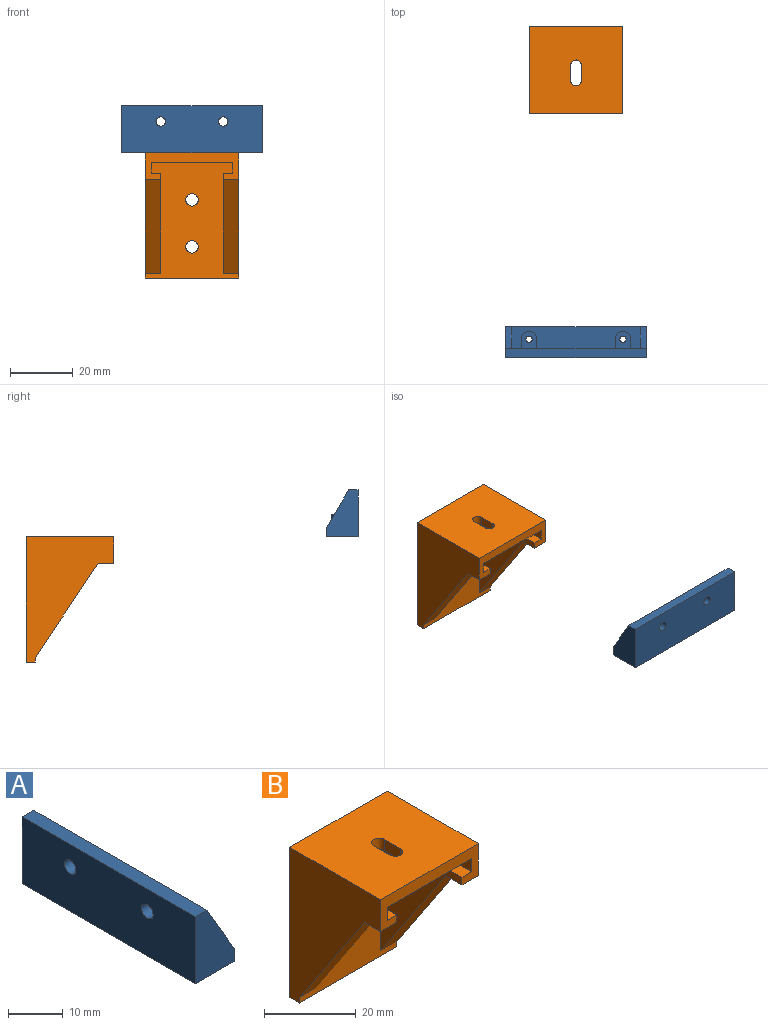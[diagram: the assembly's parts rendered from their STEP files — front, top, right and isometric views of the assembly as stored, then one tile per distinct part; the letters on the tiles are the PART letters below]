
ASSEMBLY  parts=2 mates=1
PART A: 24 faces, bbox 10x45x15 mm
  f0: plane 41x7mm, normal (0,0,1), area 237.4mm2, adj f1,f5,f12,f13,f14,f16,f17,f18
  f1: plane 41x12mm, normal (1,0,0), area 437.9mm2, adj f0,f2,f8,f9,f13,f14,f15,f16
  f2: plane 45x3mm, normal (0,0,1), area 135mm2, adj f1,f3,f6,f7,f20,f22
  f3: plane 45x15mm, normal (-1,0,0), area 660.9mm2, adj f2,f4,f6,f7,f8,f9
  f4: plane 45x10mm, normal (0,0,-1), area 443.7mm2, adj f3,f5,f6,f7,f10,f11
  f5: plane 45x3mm, normal (1,0,0), area 135mm2, adj f0,f4,f6,f7,f20,f22
  f6: plane 15x10mm, normal (0,-1,0), area 108mm2, adj f2,f3,f4,f5,f20
  f7: plane 15x10mm, normal (0,1,0), area 108mm2, adj f2,f3,f4,f5,f22
  f8: cylinder r=1.5mm len=3mm, axis (1,0,0), area 28.3mm2, adj f1,f3
  f9: cylinder r=1.5mm len=3mm, axis (1,0,0), area 28.3mm2, adj f1,f3
  f10: cylinder r=1mm len=7mm, axis (0,0,1), area 44mm2, adj f4,f19
  f11: cylinder r=1mm len=7mm, axis (0,0,1), area 44mm2, adj f4,f15
  f12: cylinder r=2.5mm len=5mm, axis (0,0,-1), area 31.4mm2, adj f0,f13,f14,f15
  f13: plane 4x3mm, normal (0,1,0), area 12mm2, adj f0,f1,f12,f15
  f14: plane 4x3mm, normal (0,-1,0), area 12mm2, adj f0,f1,f12,f15
  f15: plane 5.5x5mm, normal (0,0,1), area 21.7mm2, adj f1,f11,f12,f13,f14
  f16: plane 4x3mm, normal (0,-1,0), area 12mm2, adj f0,f1,f17,f19
  f17: cylinder r=2.5mm len=5mm, axis (0,0,-1), area 31.4mm2, adj f0,f16,f18,f19
  f18: plane 4x3mm, normal (0,1,0), area 12mm2, adj f0,f1,f17,f19
  f19: plane 5.5x5mm, normal (0,0,1), area 21.7mm2, adj f1,f10,f16,f17,f18
  f20: plane 12x7mm, normal (0.86,0,0.5), area 27.8mm2, adj f2,f5,f6,f21
  f21: plane 12x7mm, normal (0,1,0), area 42mm2, adj f0,f1,f20
  f22: plane 12x7mm, normal (0.86,0,0.5), area 27.8mm2, adj f2,f5,f7,f23
  f23: plane 12x7mm, normal (0,-1,0), area 42mm2, adj f0,f1,f22
PART B: 24 faces, bbox 30x28x40 mm
  f0: plane 26x25mm, normal (0,0,-1), area 624.9mm2, adj f2,f9,f10,f17,f20,f21,f22,f23
  f1: plane 30x28mm, normal (0,0,1), area 814.9mm2, adj f3,f7,f8,f9,f20,f21,f22,f23
  f2: plane 37x30mm, normal (0,-1,0), area 750.9mm2, adj f0,f3,f4,f5,f6,f7,f10,f11
  f3: plane 40x28mm, normal (-1,0,0), area 632.5mm2, adj f1,f2,f4,f8,f9,f14,f18
  f4: plane 30x3mm, normal (0,0,-1), area 90mm2, adj f2,f3,f7,f8
  f5: cylinder r=2mm len=4mm, axis (0,1,0), area 37.7mm2, adj f2,f8
  f6: cylinder r=2mm len=4mm, axis (0,1,0), area 37.7mm2, adj f2,f8
  f7: plane 40x28mm, normal (1,0,0), area 632.5mm2, adj f1,f2,f4,f8,f9,f13,f19
  f8: plane 40x30mm, normal (0,1,0), area 1174.9mm2, adj f1,f3,f4,f5,f6,f7
  f9: plane 30x8.5mm, normal (0,-1,0), area 124mm2, adj f0,f1,f3,f7,f10,f11,f12,f13
  f10: plane 25x3.5mm, normal (-1,0,0), area 87.5mm2, adj f0,f2,f9,f11
  f11: plane 25x3mm, normal (0,0,1), area 75mm2, adj f2,f9,f10,f12
  f12: plane 32x25mm, normal (-1,0,0), area 350mm2, adj f2,f9,f11,f13,f19
  f13: plane 5x5mm, normal (0,0,-1), area 25mm2, adj f7,f9,f12,f19
  f14: plane 5x5mm, normal (0,0,-1), area 25mm2, adj f3,f9,f15,f18
  f15: plane 32x25mm, normal (1,0,0), area 350mm2, adj f2,f9,f14,f16,f18
  f16: plane 25x3mm, normal (0,0,1), area 75mm2, adj f2,f9,f15,f17
  f17: plane 25x3.5mm, normal (1,0,0), area 87.5mm2, adj f0,f2,f9,f16
  f18: plane 30x20mm, normal (0,-0.83,-0.55), area 180.3mm2, adj f2,f3,f14,f15
  f19: plane 30x20mm, normal (0,-0.83,-0.55), area 180.3mm2, adj f2,f7,f12,f13
  f20: plane 5x3mm, normal (-1,0,0), area 15mm2, adj f0,f1,f21,f23
  f21: cylinder r=1.65mm len=3.3mm, axis (0,0,1), area 15.6mm2, adj f0,f1,f20,f22
  f22: plane 5x3mm, normal (1,0,0), area 15mm2, adj f0,f1,f21,f23
  f23: cylinder r=1.65mm len=3.3mm, axis (0,0,1), area 15.6mm2, adj f0,f1,f20,f22
PLACE A rot(axis=(0,0,1),90deg) t=(69.67,-129.46,15.7)mm
PLACE B t=(69.67,-23.46,15.7)mm
MATE fastened A.f4 <-> B.f1  axis (0,0,1) through (92.17,-129.46,15.7)mm
